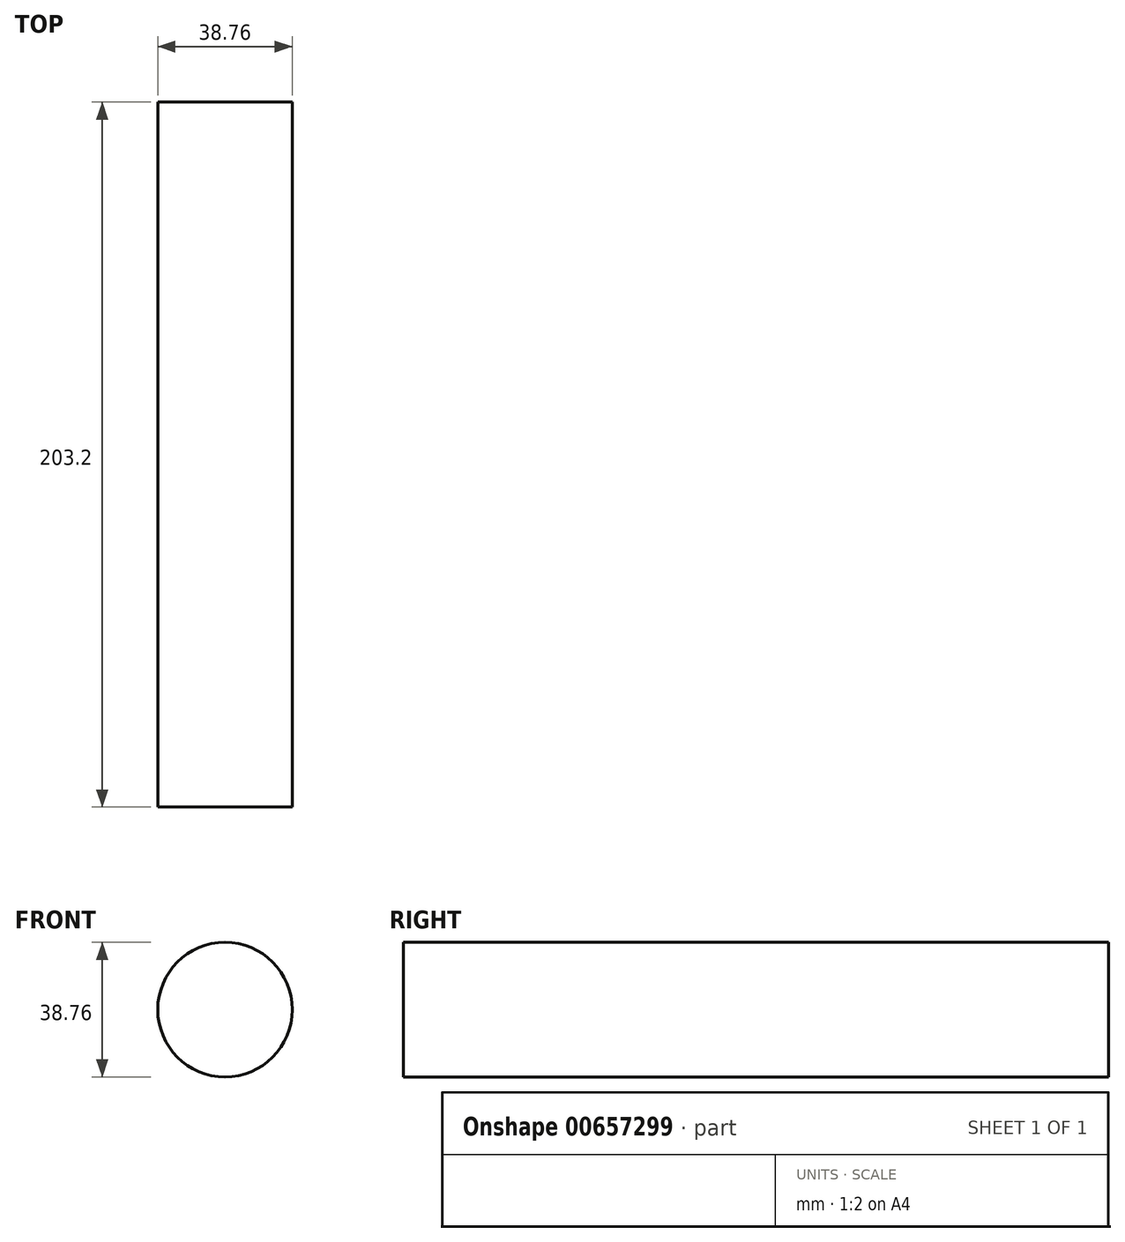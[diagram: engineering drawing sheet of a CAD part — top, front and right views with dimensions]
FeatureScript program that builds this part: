
annotation { "Feature Type Name" : "Feature", "Feature Type Description" : "" }
export const myFeature = defineFeature(function(context is Context, id is Id, definition is map)
    precondition{}
    {
        {
            var Q0;
            Q0=qCreatedBy(makeId("Front.planeOp"),FACE);
            var sketch = newSketch(context, id + "F0", { "sketchPlane" : qUnion([Q0])});
            skCircle(sketch, "E0", {"center": v(0, 0) * mm, "radius": 19.38 * mm});
            skSolve(sketch);
        }
        {
            var Q0;
            Q0 = qSketchRegion(id + "F0", true);
            extrude(context, id + "F1", {"entities" : qUnion([Q0]), "depth" : 203.2 * mm, "offsetDistance" : 25.4 * mm});
        }
    });
